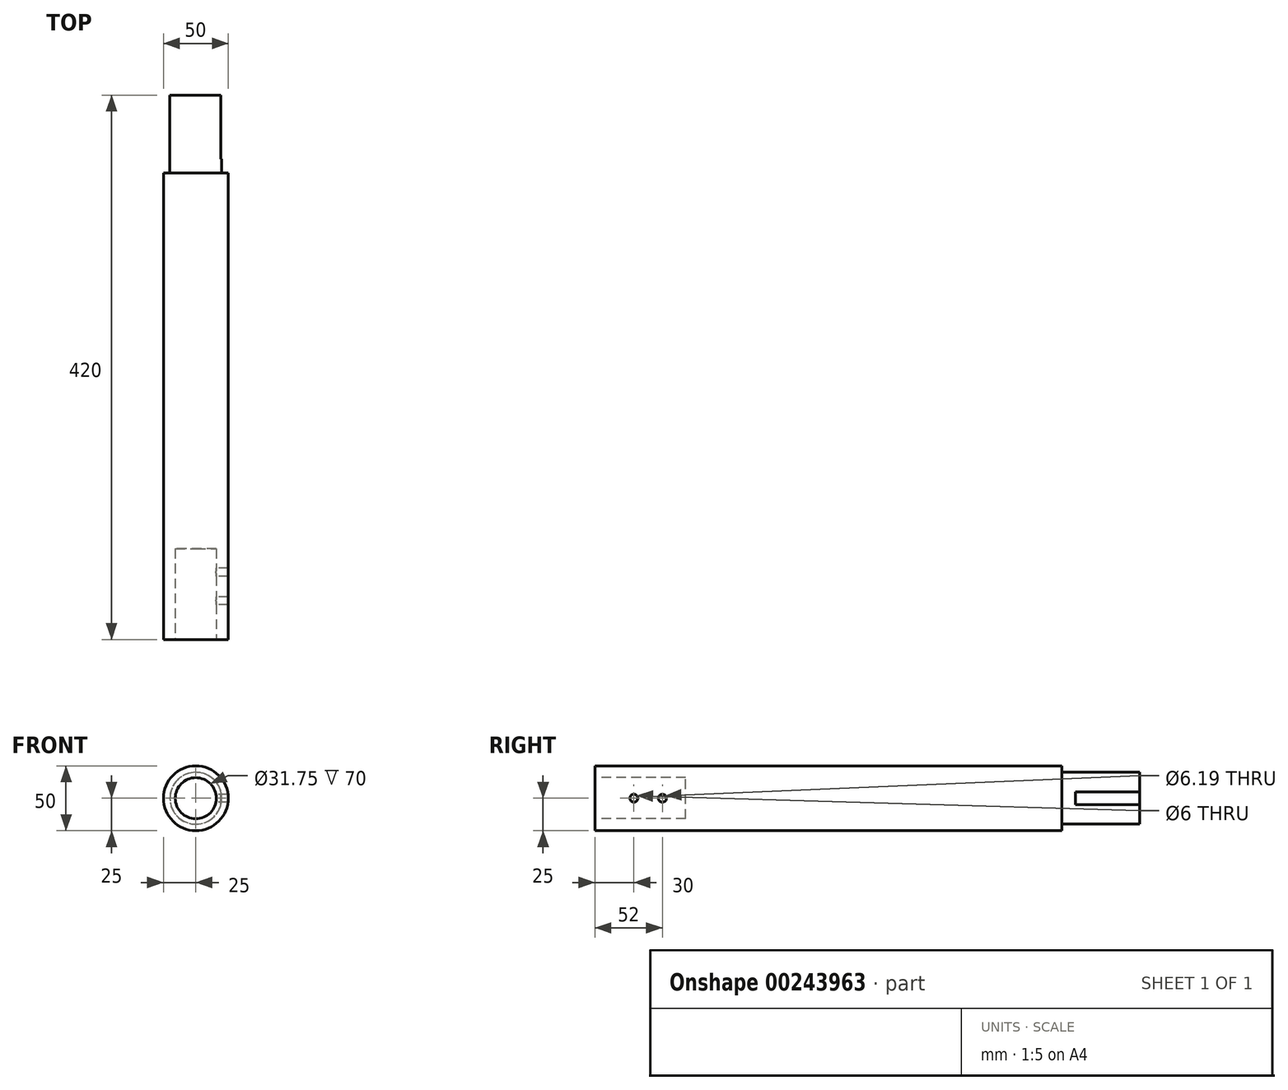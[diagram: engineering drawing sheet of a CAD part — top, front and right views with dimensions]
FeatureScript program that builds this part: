
annotation { "Feature Type Name" : "Feature", "Feature Type Description" : "" }
export const myFeature = defineFeature(function(context is Context, id is Id, definition is map)
    precondition{}
    {
        {
            var Q0;
            Q0=qCreatedBy(makeId("Front.planeOp"),FACE);
            var sketch = newSketch(context, id + "F0", { "sketchPlane" : qUnion([Q0])});
            skCircle(sketch, "E0", {"center": v(0, 0) * mm, "radius": 25 * mm});
            skSolve(sketch);
        }
        {
            var Q0;
            Q0 = qSketchRegion(id + "F0", true);
            extrude(context, id + "F1", {"entities" : qUnion([Q0]), "depth" : 420 * mm});
        }
        {
            var Q0;
            Q0=makeQuery(id+"F1.opExtrude","CAP_FACE",FACE,{"disambiguationData":[OSD([sQuery(id+"F0.wireOp",EDGE,"E0")])],"isStart":false});
            var sketch = newSketch(context, id + "F2", { "sketchPlane" : qUnion([Q0])});
            skCircle(sketch, "E1", {"center": v(0, 0) * mm, "radius": 15.88 * mm});
            skSolve(sketch);
        }
        {
            var Q0;
            Q0 = qSketchRegion(id + "F2", true);
            extrude(context, id + "F3", {"entities" : qUnion([Q0]), "operationType" : NewBodyOperationType.REMOVE, "oppositeDirection" : true, "depth" : 70 * mm});
        }
        {
            var Q0;
            Q0=qCreatedBy(makeId("Right.planeOp"),FACE);
            var sketch = newSketch(context, id + "F4", { "sketchPlane" : qUnion([Q0])});
            skCircle(sketch, "E2", {"center": v(-390, 0) * mm, "radius": 3 * mm});
            skCircle(sketch, "E3", {"center": v(-368, 0) * mm, "radius": 3.1 * mm});
            skSolve(sketch);
        }
        {
            var Q0;
            Q0 = qSketchRegion(id + "F4", true);
            extrude(context, id + "F5", {"entities" : qUnion([Q0]), "operationType" : NewBodyOperationType.REMOVE, "depth" : 48.2 * mm});
        }
        {
            var Q0;
            Q0=makeQuery(id+"F1.opExtrude","CAP_FACE",FACE,{"disambiguationData":[OSD([sQuery(id+"F0.wireOp",EDGE,"E0")])],"isStart":true});
            var sketch = newSketch(context, id + "F6", { "sketchPlane" : qUnion([Q0])});
            skCircle(sketch, "E4", {"center": v(0, 0) * mm, "radius": 20 * mm});
            skSolve(sketch);
        }
        {
            var Q0;
            Q0=makeQuery(id+"F6.imprint","IMPRINT",FACE,{"disambiguationData":[TD([[makeQuery(id+"F6.imprint","IMPRINT",EDGE,{"derivedFrom":sQuery(id+"F6.wireOp",EDGE,"E4")}),-1.0]])]});
            extrude(context, id + "F7", {"entities" : qUnion([Q0]), "operationType" : NewBodyOperationType.REMOVE, "oppositeDirection" : true, "depth" : 60 * mm});
        }
        {
            var Q0;
            Q0=qCreatedBy(makeId("Right.planeOp"),FACE);
            cPlane(context, id + "F8", {"entities" : qUnion([Q0]), "cplaneType" : CPlaneType.OFFSET, "offset" : 20 * mm, "width" : 150 * mm, "height" : 150 * mm});
        }
        {
            var Q0;
            Q0=qCreatedBy(id+"F8.planeOp",FACE);
            var sketch = newSketch(context, id + "F9", { "sketchPlane" : qUnion([Q0])});
            skLineSegment(sketch, "E5.bottom", {"start": v(-49.35, -5) * mm, "end": v(49.35, -5) * mm});
            skLineSegment(sketch, "E5.top", {"start": v(-49.35, 5) * mm, "end": v(49.35, 5) * mm});
            skLineSegment(sketch, "E5.left", {"start": v(-49.35, -5) * mm, "end": v(-49.35, 5) * mm});
            skLineSegment(sketch, "E5.right", {"start": v(49.35, -5) * mm, "end": v(49.35, 5) * mm});
            skPoint(sketch, "E5.middle", {"position": v(0, 0) * mm});
            skSolve(sketch);
        }
        {
            var Q0;
            Q0 = qSketchRegion(id + "F9", true);
            extrude(context, id + "F10", {"entities" : qUnion([Q0]), "operationType" : NewBodyOperationType.REMOVE, "oppositeDirection" : true, "depth" : .8 * mm});
        }
    });
